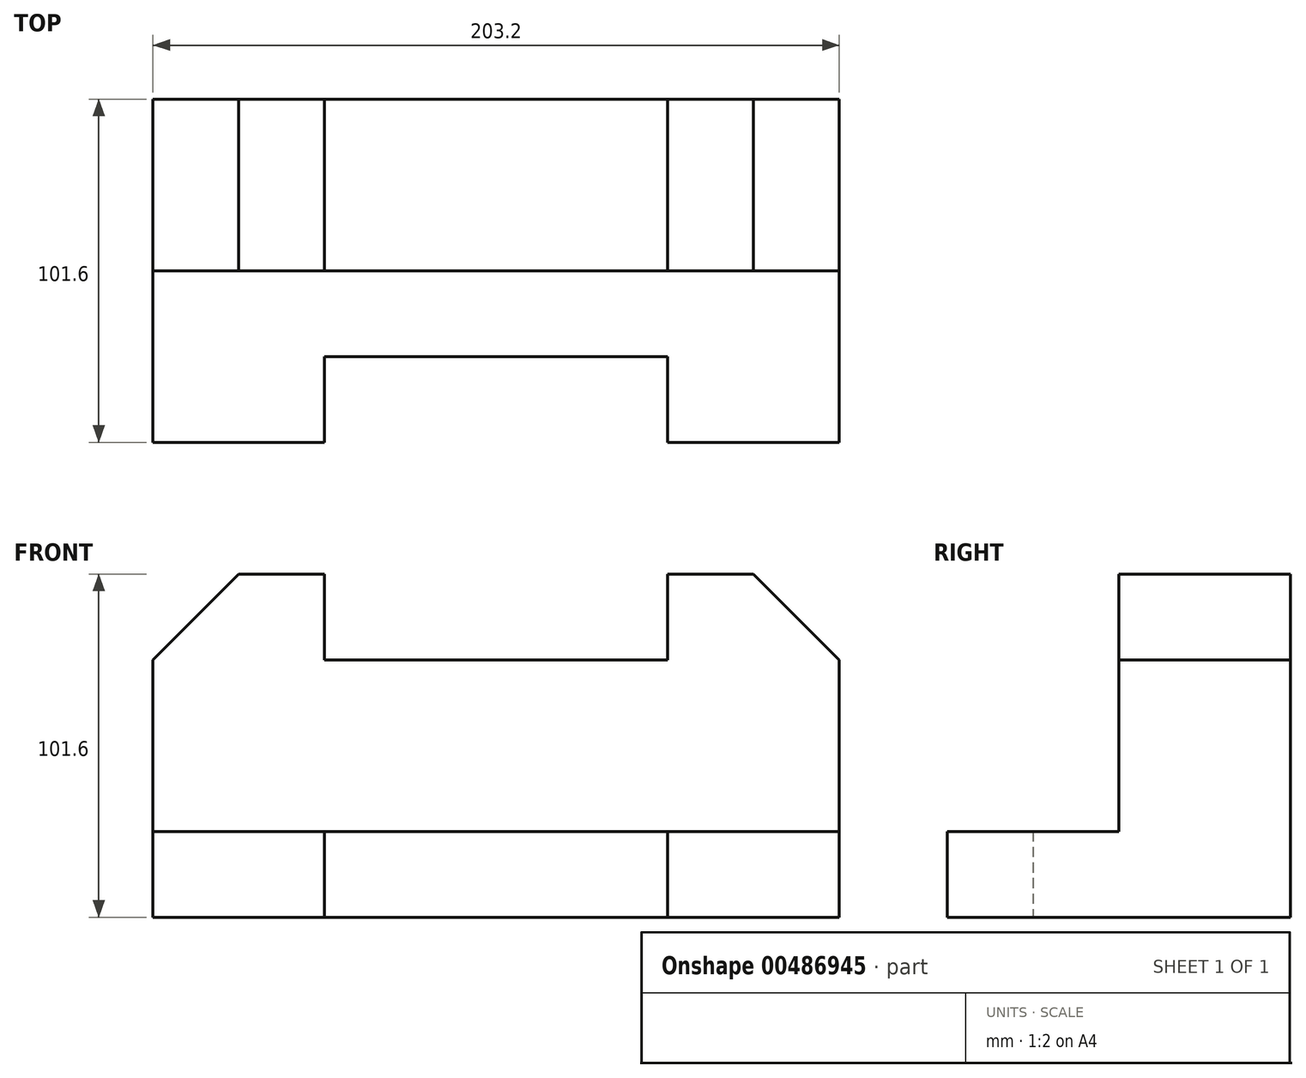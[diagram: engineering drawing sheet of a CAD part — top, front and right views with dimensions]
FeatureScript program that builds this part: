
annotation { "Feature Type Name" : "Feature", "Feature Type Description" : "" }
export const myFeature = defineFeature(function(context is Context, id is Id, definition is map)
    precondition{}
    {
        {
            var Q0;
            Q0=qCreatedBy(makeId("Front.planeOp"),FACE);
            var sketch = newSketch(context, id + "F0", { "sketchPlane" : qUnion([Q0])});
            skLineSegment(sketch, "E0.bottom", {"start": v(-101.6, -50.8) * mm, "end": v(101.6, -50.8) * mm});
            skLineSegment(sketch, "E0.top", {"start": v(-101.6, 50.8) * mm, "end": v(101.6, 50.8) * mm});
            skLineSegment(sketch, "E0.left", {"start": v(-101.6, -50.8) * mm, "end": v(-101.6, 50.8) * mm});
            skLineSegment(sketch, "E0.right", {"start": v(101.6, -50.8) * mm, "end": v(101.6, 50.8) * mm});
            skPoint(sketch, "E0.middle", {"position": v(0, 0) * mm});
            skSolve(sketch);
        }
        {
            var Q0;
            Q0 = qSketchRegion(id + "F0", true);
            extrude(context, id + "F1", {"entities" : qUnion([Q0]), "depth" : 101.6 * mm});
        }
        {
            var Q0;
            Q0=makeQuery(id+"F1.opExtrude","CAP_FACE",FACE,{"disambiguationData":[OSD([sQuery(id+"F0.wireOp",EDGE,"E0.bottom"),sQuery(id+"F0.wireOp",EDGE,"E0.top"),sQuery(id+"F0.wireOp",EDGE,"E0.left"),sQuery(id+"F0.wireOp",EDGE,"E0.right")])],"isStart":false});
            var sketch = newSketch(context, id + "F2", { "sketchPlane" : qUnion([Q0])});
            skLineSegment(sketch, "E1.bottom", {"start": v(101.6, 50.8) * mm, "end": v(-101.6, 50.8) * mm});
            skLineSegment(sketch, "E1.top", {"start": v(101.6, -25.4) * mm, "end": v(-101.6, -25.4) * mm});
            skLineSegment(sketch, "E1.left", {"start": v(101.6, 50.8) * mm, "end": v(101.6, -25.4) * mm});
            skLineSegment(sketch, "E1.right", {"start": v(-101.6, 50.8) * mm, "end": v(-101.6, -25.4) * mm});
            skSolve(sketch);
        }
        {
            var Q0;
            Q0 = qSketchRegion(id + "F2", true);
            extrude(context, id + "F3", {"entities" : qUnion([Q0]), "operationType" : NewBodyOperationType.REMOVE, "oppositeDirection" : true, "depth" : 50.8 * mm});
        }
        {
            var Q0;
            Q0=makeQuery(id+"F1.opExtrude","CAP_FACE",FACE,{"disambiguationData":[OSD([sQuery(id+"F0.wireOp",EDGE,"E0.bottom"),sQuery(id+"F0.wireOp",EDGE,"E0.top"),sQuery(id+"F0.wireOp",EDGE,"E0.left"),sQuery(id+"F0.wireOp",EDGE,"E0.right")])],"isStart":false});
            var sketch = newSketch(context, id + "F4", { "sketchPlane" : qUnion([Q0])});
            skLineSegment(sketch, "E2.bottom", {"start": v(-50.8, -25.4) * mm, "end": v(50.8, -25.4) * mm});
            skLineSegment(sketch, "E2.top", {"start": v(-50.8, -50.8) * mm, "end": v(50.8, -50.8) * mm});
            skLineSegment(sketch, "E2.left", {"start": v(-50.8, -25.4) * mm, "end": v(-50.8, -50.8) * mm});
            skLineSegment(sketch, "E2.right", {"start": v(50.8, -25.4) * mm, "end": v(50.8, -50.8) * mm});
            skPoint(sketch, "E2.middle", {"position": v(0, -38.1) * mm});
            skSolve(sketch);
        }
        {
            var Q0;
            Q0 = qSketchRegion(id + "F4", true);
            extrude(context, id + "F5", {"entities" : qUnion([Q0]), "operationType" : NewBodyOperationType.REMOVE, "oppositeDirection" : true, "depth" : 25.4 * mm});
        }
        {
            var Q0;
            Q0=makeQuery(id+"F3.boolean.opBoolean","COPY",FACE,{"derivedFrom":makeQuery(id+"F3.opExtrude","CAP_FACE",FACE,{"disambiguationData":[OSD([sQuery(id+"F2.wireOp",EDGE,"E1.bottom"),sQuery(id+"F2.wireOp",EDGE,"E1.top"),sQuery(id+"F2.wireOp",EDGE,"E1.left"),sQuery(id+"F2.wireOp",EDGE,"E1.right")])],"isStart":false})});
            var sketch = newSketch(context, id + "F6", { "sketchPlane" : qUnion([Q0])});
            skLineSegment(sketch, "E3.bottom", {"start": v(-50.8, 50.8) * mm, "end": v(50.8, 50.8) * mm});
            skLineSegment(sketch, "E3.top", {"start": v(-50.8, 25.4) * mm, "end": v(50.8, 25.4) * mm});
            skLineSegment(sketch, "E3.left", {"start": v(-50.8, 50.8) * mm, "end": v(-50.8, 25.4) * mm});
            skLineSegment(sketch, "E3.right", {"start": v(50.8, 50.8) * mm, "end": v(50.8, 25.4) * mm});
            skPoint(sketch, "E3.middle", {"position": v(0, 38.1) * mm});
            skPoint(sketch, "E3.middle.positionSnap0", {"position": v(0, 50.8) * mm});
            skPoint(sketch, "E3.centerSnap0", {"position": v(0, 50.8) * mm});
            skSolve(sketch);
        }
        {
            var Q0;
            Q0 = qSketchRegion(id + "F6", true);
            extrude(context, id + "F7", {"entities" : qUnion([Q0]), "operationType" : NewBodyOperationType.REMOVE, "oppositeDirection" : true, "depth" : 50.8 * mm});
        }
        {
            var Q0;
            Q0=makeQuery(id+"F3.boolean.opBoolean","COPY",FACE,{"derivedFrom":makeQuery(id+"F3.opExtrude","CAP_FACE",FACE,{"disambiguationData":[OSD([sQuery(id+"F2.wireOp",EDGE,"E1.bottom"),sQuery(id+"F2.wireOp",EDGE,"E1.top"),sQuery(id+"F2.wireOp",EDGE,"E1.left"),sQuery(id+"F2.wireOp",EDGE,"E1.right")])],"isStart":false})});
            var sketch = newSketch(context, id + "F8", { "sketchPlane" : qUnion([Q0])});
            skPoint(sketch, "E4.start.orphan", {"position": v(76.2, 50.8) * mm});
            skLineSegment(sketch, "E5", {"start": v(76.2, 50.8) * mm, "end": v(101.6, 50.8) * mm});
            skLineSegment(sketch, "E6", {"start": v(101.6, 50.8) * mm, "end": v(101.6, 25.4) * mm});
            skLineSegment(sketch, "E7", {"start": v(101.6, 25.4) * mm, "end": v(76.2, 50.8) * mm});
            skLineSegment(sketch, "E8", {"start": v(-76.2, 50.8) * mm, "end": v(-101.6, 50.8) * mm});
            skLineSegment(sketch, "E9", {"start": v(-101.6, 50.8) * mm, "end": v(-101.6, 25.4) * mm});
            skLineSegment(sketch, "E10", {"start": v(-101.6, 25.4) * mm, "end": v(-76.2, 50.8) * mm});
            skSolve(sketch);
        }
        {
            var Q0;
            Q0 = qSketchRegion(id + "F8", true);
            extrude(context, id + "F9", {"entities" : qUnion([Q0]), "operationType" : NewBodyOperationType.REMOVE, "oppositeDirection" : true, "depth" : 50.8 * mm});
        }
    });
